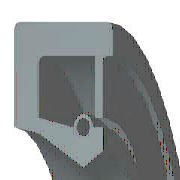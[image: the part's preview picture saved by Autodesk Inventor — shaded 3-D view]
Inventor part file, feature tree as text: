
AUTODESK INVENTOR PART (.ipt)
format: ipt  version: 2023.2 (Build 272271030, 271C)  size: 206,336 bytes
history: native  units: mm (DEFAULTED — no unit token found)
features: plane x3, sketch x2, other x1, fillet x1
ambient origin geometry x7: Origin, YZ Plane, XY Plane, X Axis, Y Axis, Z Axis, Center Point
bodies: Solid1 (feature_tree)
feature tree (7):
  plane  "WorkPlane2"
  sketch  "Sketch1"  dims[d1=8.0mm]
  other  "WorkPoint1"
  plane  "WorkPlane3"
  fillet  "Fillet1"  [1 undecoded]
  plane  "WorkPlane1"
  sketch  "Sketch2"  dims[d2=7.0mm d3=0.4mm d4=0.35mm d5=0.4mm d6=0.35mm d7=0.4mm d8=0.35mm d9=0.8mm d10=0.7mm d11=0.8mm d12=0.7mm d13=2.0mm d14=2.7mm d15=2.0mm d16=2.7mm d17=3.333333mm d18=2.916667mm d19=2.0mm d20=1.75mm d21=1.0mm d22=1.35mm d23=0.8mm d24=0.7mm d25=0.5mm d26=0.675mm d27=1.0mm d28=1.35mm d29=0.5mm d30=0.675mm d31=360.0deg d32=0.35mm d36=0.0mm]
note: 1 required parameter value undecoded (feature->parameter linkage not recoverable at this tier; creation-order binding heuristic only, values carry confidence <= 0.55)
